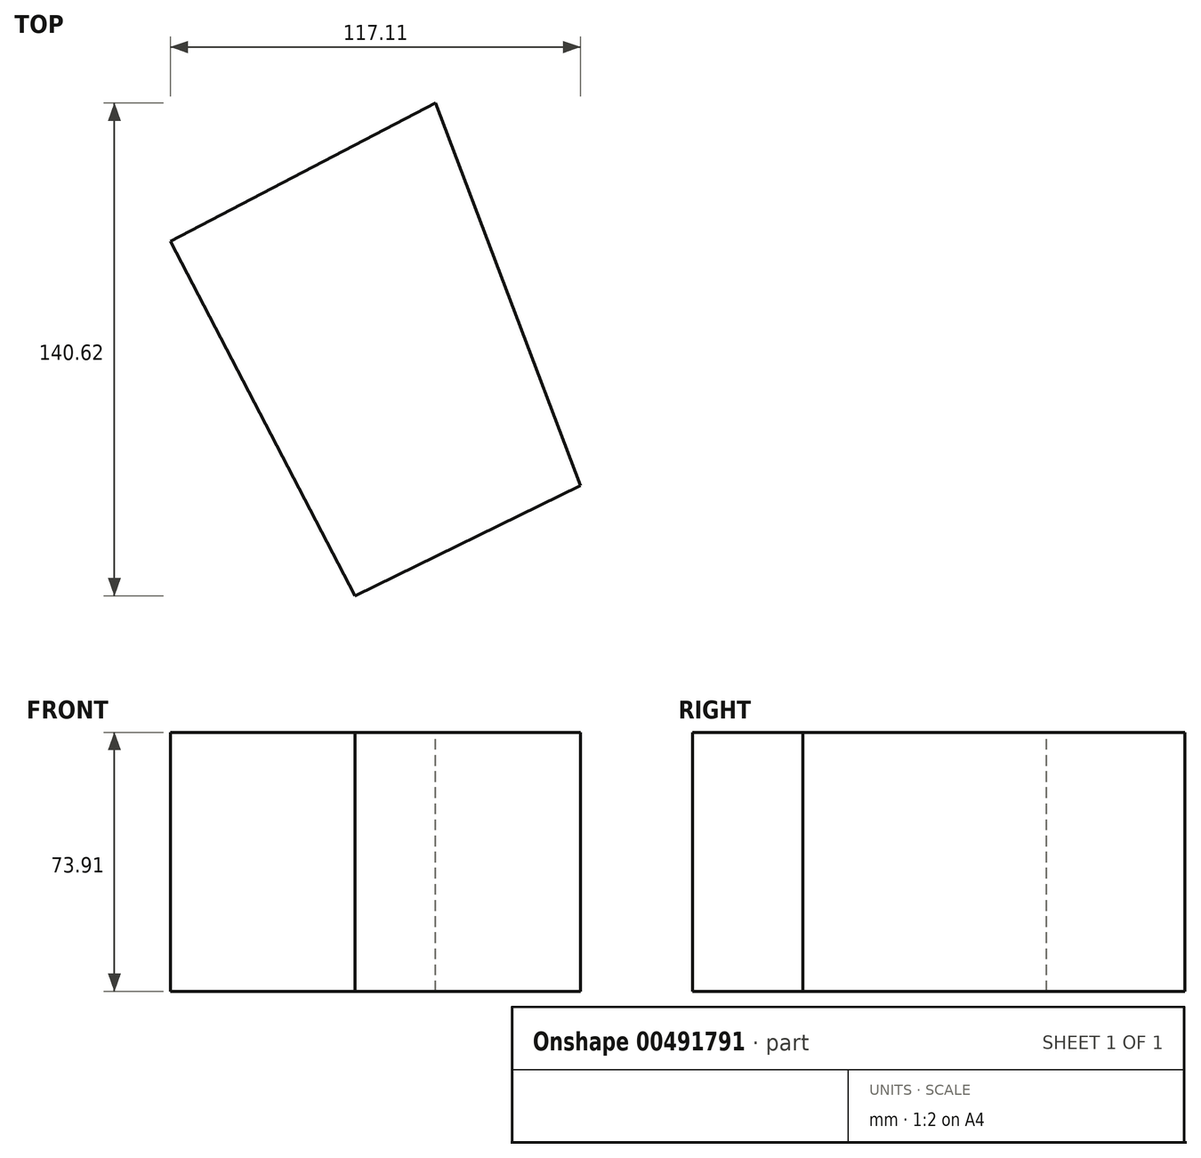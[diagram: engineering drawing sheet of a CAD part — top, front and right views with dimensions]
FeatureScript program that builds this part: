
annotation { "Feature Type Name" : "Feature", "Feature Type Description" : "" }
export const myFeature = defineFeature(function(context is Context, id is Id, definition is map)
    precondition{}
    {
        {
            var Q0;
            Q0=qCreatedBy(makeId("Top.planeOp"),FACE);
            var sketch = newSketch(context, id + "F0", { "sketchPlane" : qUnion([Q0])});
            skLineSegment(sketch, "E0", {"start": v(58.8, -41.16) * mm, "end": v(17.4, 67.97) * mm});
            skLineSegment(sketch, "E1", {"start": v(17.4, 67.97) * mm, "end": v(-58.32, 28.46) * mm});
            skLineSegment(sketch, "E2", {"start": v(-58.32, 28.46) * mm, "end": v(-5.57, -72.65) * mm});
            skLineSegment(sketch, "E3", {"start": v(-5.57, -72.65) * mm, "end": v(58.8, -41.16) * mm});
            skSolve(sketch);
        }
        {
            var Q0;
            Q0=makeQuery(id+"F0.imprint","IMPRINT",FACE,{"disambiguationData":[TD([[makeQuery(id+"F0.imprint","IMPRINT",EDGE,{"derivedFrom":sQuery(id+"F0.wireOp",EDGE,"E0")}),1.0]])]});
            extrude(context, id + "F1", {"entities" : qUnion([Q0]), "oppositeDirection" : true, "depth" : 73.9 * mm});
        }
    });
